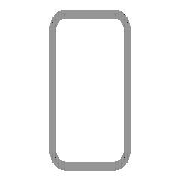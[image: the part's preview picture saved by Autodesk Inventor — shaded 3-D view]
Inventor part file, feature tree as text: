
AUTODESK INVENTOR PART (.ipt)
format: ipt  version: 2025 (Build 290162010, 162A)  size: 133,120 bytes
history: native  units: mm (DEFAULTED — no unit token found)
features: other x4, sketch x1, plane x1
ambient origin geometry x8: Origin, YZ Plane, XZ Plane, XY Plane, X Axis, Y Axis, Z Axis, Center Point
bodies: Solid1 (feature_tree), Body (feature_tree)
feature tree (6):
  parser-record x1  (decoder bookkeeping rows leaked as tree rows — omitted from the tree; the rows remain in map.json)
  other  "Driven Length"
  other  "Start Plane"
  other  "End Plane"
  sketch  "Sketch3"  dims[d3=4382.0mm d4=0.0mm d7=4.0mm d9=20.0mm d11=40.0mm d12=2.0mm d13=-0.0mm d14=4382.0mm d15=10.0mm d16=20.0mm d17=90.0deg d18=4382.0mm]
  plane  "Work Plane3"
